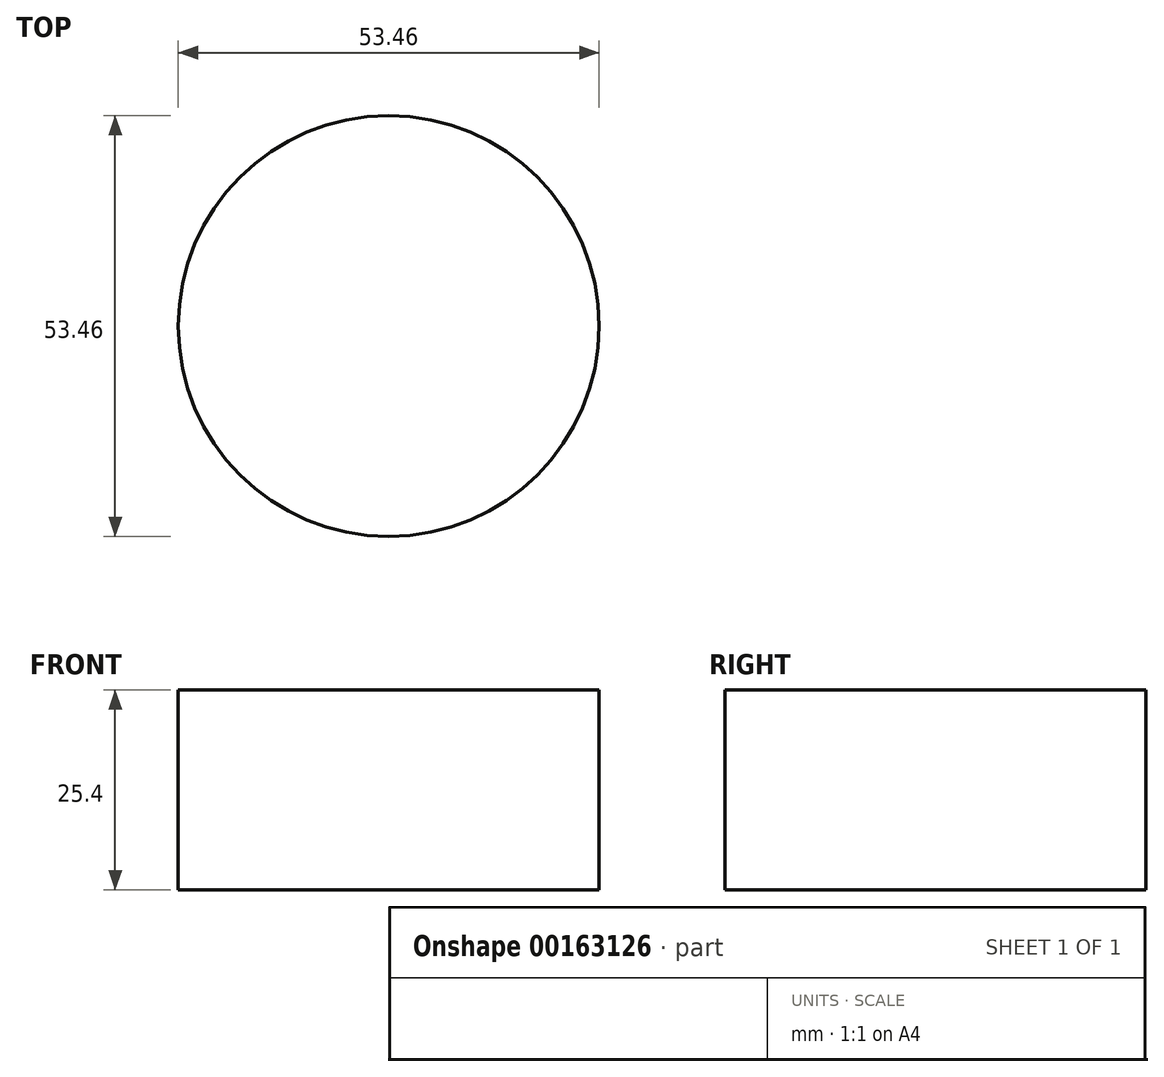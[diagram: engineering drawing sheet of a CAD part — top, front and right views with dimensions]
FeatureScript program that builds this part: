
annotation { "Feature Type Name" : "Feature", "Feature Type Description" : "" }
export const myFeature = defineFeature(function(context is Context, id is Id, definition is map)
    precondition{}
    {
        {
            var Q0;
            Q0=qCreatedBy(makeId("Top.planeOp"),FACE);
            var sketch = newSketch(context, id + "F0", { "sketchPlane" : qUnion([Q0])});
            skCircle(sketch, "E0", {"center": v(0, 0) * mm, "radius": 26.73 * mm});
            skSolve(sketch);
        }
        {
            var Q0;
            Q0 = qSketchRegion(id + "F0", true);
            extrude(context, id + "F1", {"entities" : qUnion([Q0]), "depth" : 25.4 * mm});
        }
    });
